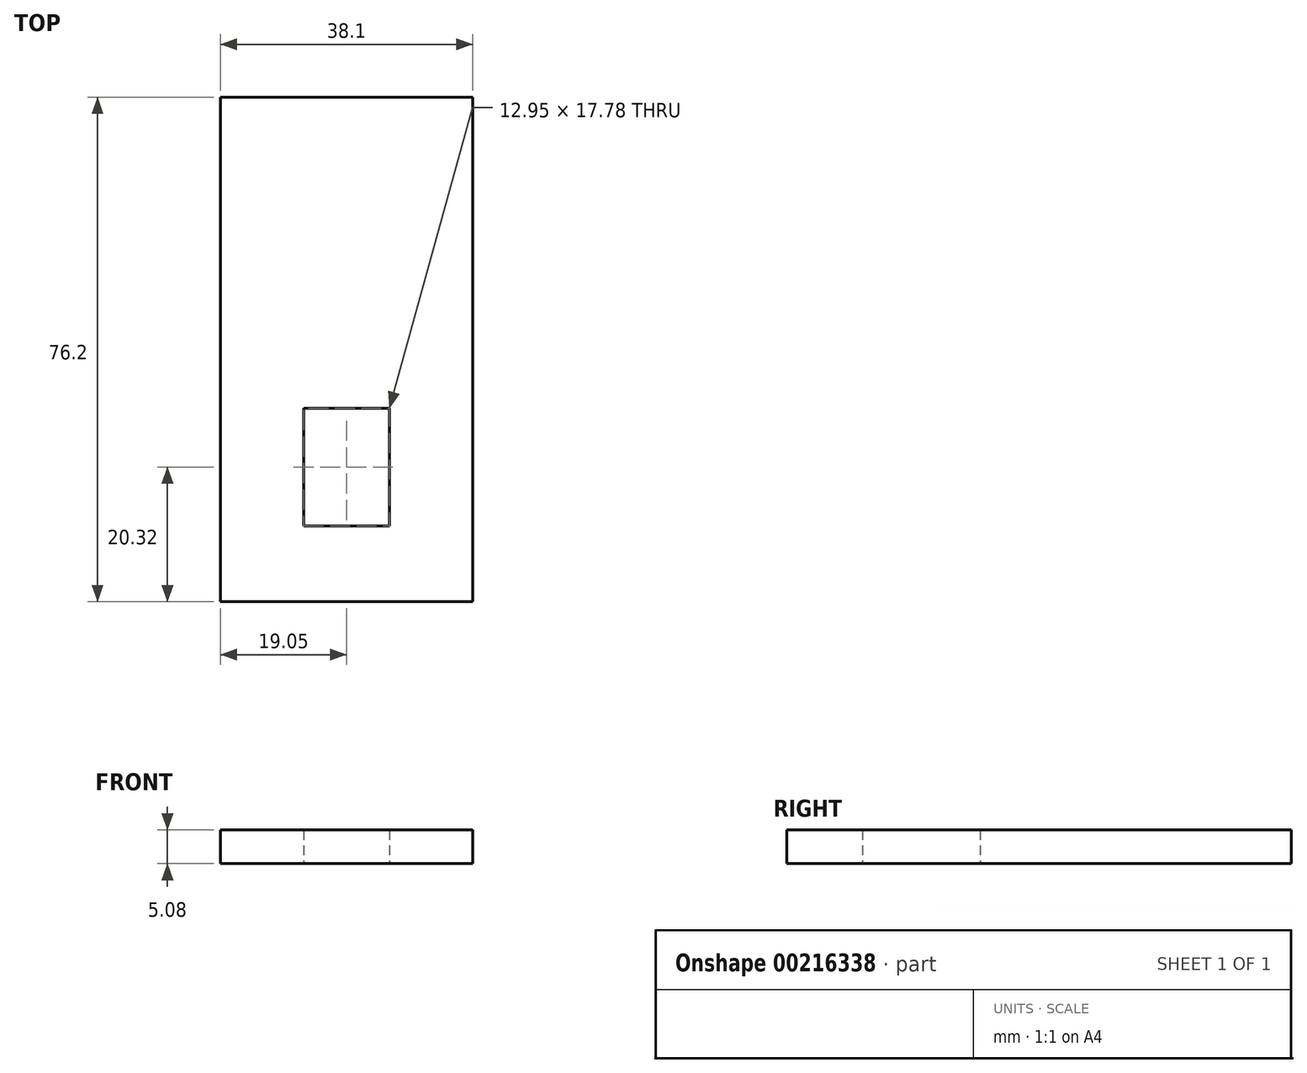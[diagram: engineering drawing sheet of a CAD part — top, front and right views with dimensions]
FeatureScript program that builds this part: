
annotation { "Feature Type Name" : "Feature", "Feature Type Description" : "" }
export const myFeature = defineFeature(function(context is Context, id is Id, definition is map)
    precondition{}
    {
        {
            var Q0;
            Q0=qCreatedBy(makeId("Top.planeOp"),FACE);
            var sketch = newSketch(context, id + "F0", { "sketchPlane" : qUnion([Q0])});
            skLineSegment(sketch, "E0.bottom", {"start": v(19.05, -38.1) * mm, "end": v(-19.05, -38.1) * mm});
            skLineSegment(sketch, "E0.top", {"start": v(19.05, 38.1) * mm, "end": v(-19.05, 38.1) * mm});
            skLineSegment(sketch, "E0.left", {"start": v(19.05, -38.1) * mm, "end": v(19.05, 38.1) * mm});
            skLineSegment(sketch, "E0.right", {"start": v(-19.05, -38.1) * mm, "end": v(-19.05, 38.1) * mm});
            skPoint(sketch, "E0.middle", {"position": v(0, 0) * mm});
            skLineSegment(sketch, "E1.bottom", {"start": v(-6.48, -8.9) * mm, "end": v(6.48, -8.9) * mm});
            skLineSegment(sketch, "E1.top", {"start": v(-6.48, -26.67) * mm, "end": v(6.48, -26.67) * mm});
            skLineSegment(sketch, "E1.left", {"start": v(-6.48, -8.9) * mm, "end": v(-6.48, -26.67) * mm});
            skLineSegment(sketch, "E1.right", {"start": v(6.48, -8.9) * mm, "end": v(6.48, -26.67) * mm});
            skPoint(sketch, "E1.middle", {"position": v(0, -17.78) * mm});
            skSolve(sketch);
        }
        {
            var Q0;
            Q0=makeQuery(id+"F0.imprint","IMPRINT",FACE,{"disambiguationData":[TD([[makeQuery(id+"F0.imprint","IMPRINT",EDGE,{"derivedFrom":sQuery(id+"F0.wireOp",EDGE,"E0.bottom")}),-1.0]])]});
            extrude(context, id + "F1", {"entities" : qUnion([Q0]), "depth" : 5.08 * mm});
        }
    });
